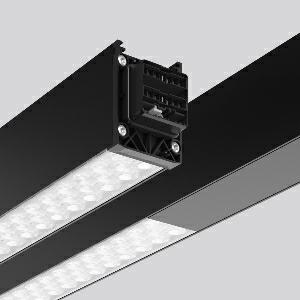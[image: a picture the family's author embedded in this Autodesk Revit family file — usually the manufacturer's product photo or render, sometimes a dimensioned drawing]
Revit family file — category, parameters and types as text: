
# Revit family: linedo_4_5m_90_10001000_954590_843_776_703_eb6d
name_source: partatom
category: Lighting Fixtures
units: mm (PartAtom-declared; Revit-internal decimal feet)

## family parameters
Cut with Voids When Loaded = No
Host = Face
Light Source = No
Part Type = Normal
Room Calculation Point = No
Round Connector Dimension = Use Diameter
Shared = No

## types (1)
- LINEDO_4,5m_90_10001000 (1 x LED Modul 840, 4100 lm, 4000)
    Apparent Load = 54 VA
    CIE Flux Codes = 73 96 99 100 100
    Color Rendering = 80
    Color Temperature = 4000
    Default Elevation = 1800 mm
    Description = LINEDO, 54 W, 8200 lm, 840, black, DALI
Continuous line luminaire, L 4547 B 58 H 76
    Height = 76 mm
    Lamp = 1 x LED Modul 840
    Lamp Light Flux = 4100 lm
    Lamp count = 1
    Length = 4547 mm
    Lifetime = 50000 h
    Luminous efficacy = 152 lm/W
    Manufacturer = RZB
    ModVariant = No
    Model = 954590.843.776.703
    Mounting Place = Ceiling
    Mounting Type = Surface mounted, Pendant
    Number of Poles = 1
    OnlyDefault = Yes
    Power Factor = 1
    Product Name = LINEDO_4,5m_90_10001000
    Product group = Surface mounted continuous line luminaire system
    ProductGroupID = 310
    Protection Class = Protection class I
    Protection Degree = IP 54
    RLX_Detail_Level = 1
    RLX_Emergency_Light_Flux = 0 lm
    RLX_Emergency_Type = 0
    RLX_Emergency_Type_DB = No
    RlxData = <blob elided: 56813 chars, md5=47884fa1>
    Socket = socket
    Standby Power = 0 W
    System Light Flux = 8200 lm
    System Power = 54 W
    Type Comments = Product without accessories
    Type Image = 954590.853.476.504.jpg
    URL = http://relux.com
    VarID = ---
    Voltage = 230 V
    Voltage Range = 220-240 V
    Weight = 0.00 kg
    Width = 58 mm

## geometry (parser evidence)
native form markers: Blend x4, Sweep x15
no freeform markers — native parametric forms only
